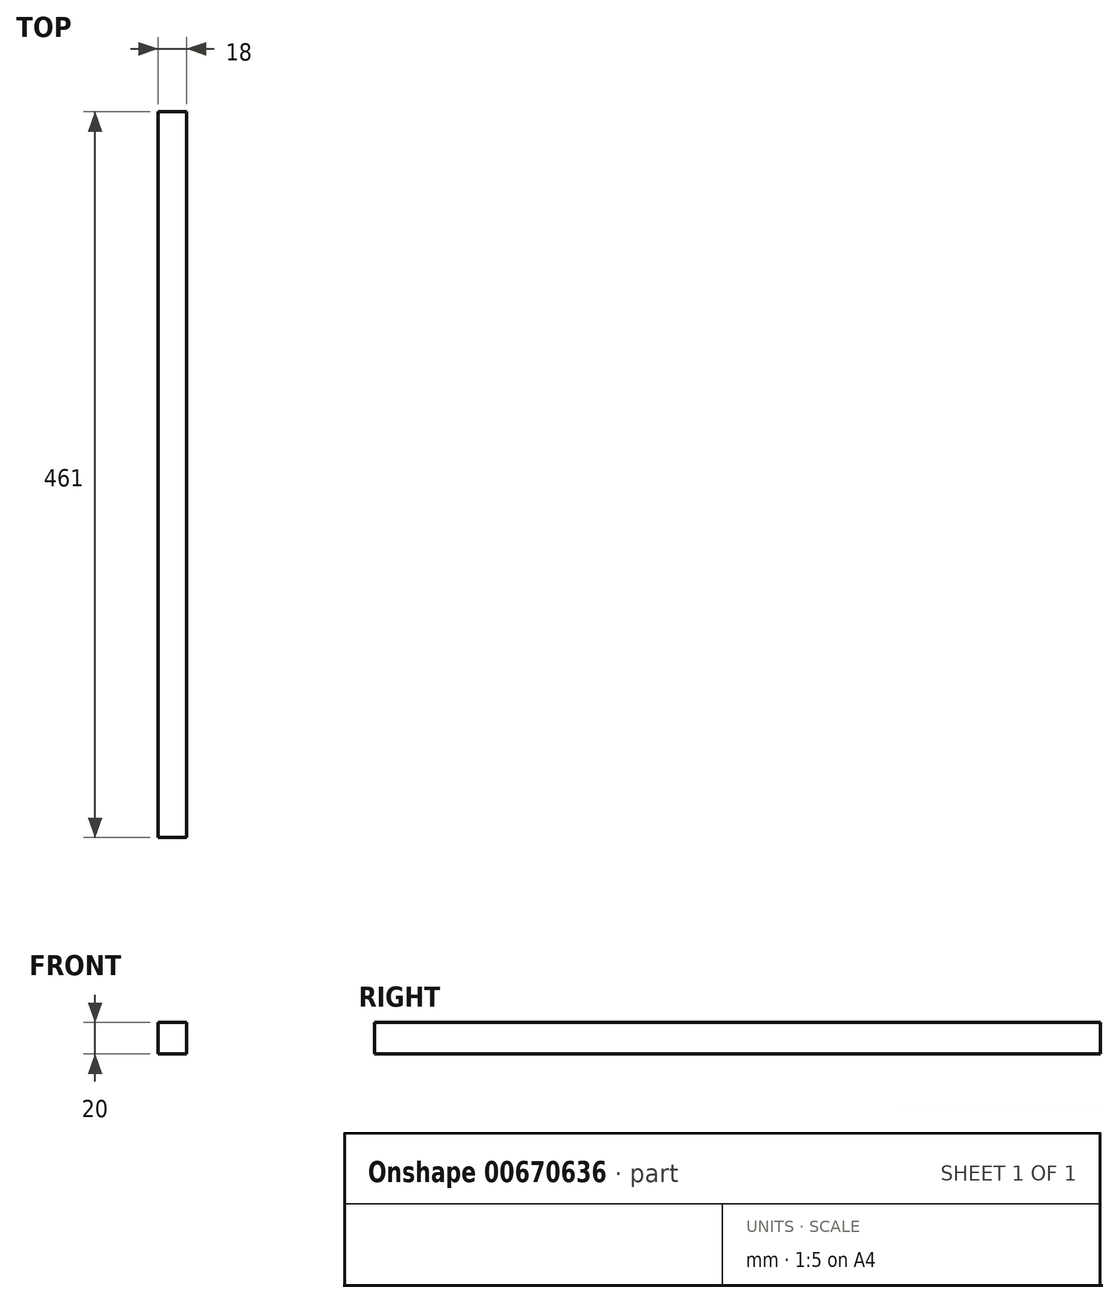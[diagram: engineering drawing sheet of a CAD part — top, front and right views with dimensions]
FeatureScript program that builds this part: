
annotation { "Feature Type Name" : "Feature", "Feature Type Description" : "" }
export const myFeature = defineFeature(function(context is Context, id is Id, definition is map)
    precondition{}
    {
        {
            var Q0;
            Q0=qCreatedBy(makeId("Top.planeOp"),FACE);
            var sketch = newSketch(context, id + "F0", { "sketchPlane" : qUnion([Q0])});
            skLineSegment(sketch, "E0.bottom", {"start": v(9, 230.5) * mm, "end": v(-9, 230.5) * mm});
            skLineSegment(sketch, "E0.top", {"start": v(9, -230.5) * mm, "end": v(-9, -230.5) * mm});
            skLineSegment(sketch, "E0.left", {"start": v(9, 230.5) * mm, "end": v(9, -230.5) * mm});
            skLineSegment(sketch, "E0.right", {"start": v(-9, 230.5) * mm, "end": v(-9, -230.5) * mm});
            skPoint(sketch, "E0.middle", {"position": v(0, 0) * mm});
            skSolve(sketch);
        }
        {
            var Q0;
            Q0 = qSketchRegion(id + "F0", true);
            extrude(context, id + "F1", {"entities" : qUnion([Q0]), "endBound" : BoundingType.SYMMETRIC, "depth" : 20 * mm, "offsetDistance" : 25 * mm});
        }
    });
